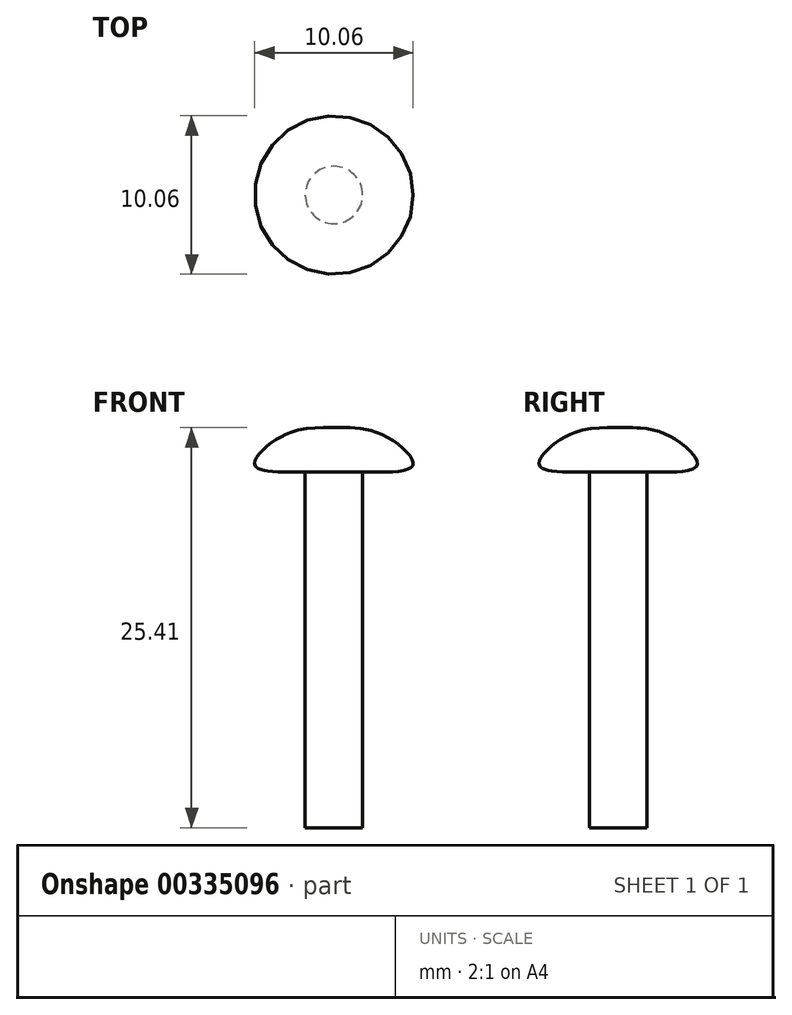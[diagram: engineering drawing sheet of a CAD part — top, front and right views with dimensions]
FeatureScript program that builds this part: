
annotation { "Feature Type Name" : "Feature", "Feature Type Description" : "" }
export const myFeature = defineFeature(function(context is Context, id is Id, definition is map)
    precondition{}
    {
        {
            var Q0;
            Q0=qCreatedBy(makeId("Front.planeOp"),FACE);
            var sketch = newSketch(context, id + "F0", { "sketchPlane" : qUnion([Q0])});
            skFitSpline(sketch, "E0", {"points": [v(0, 25.4) * mm, v(3.16, 24.93) * mm, v(5.03, 23.06) * mm, v(1.82, 22.6) * mm], "startDerivative": vector(9.1, 0.23) * mm, "endDerivative": vector(-13.32, 0.24) * mm});
            skLineSegment(sketch, "E1", {"start": v(1.82, 22.6) * mm, "end": v(1.82, 0) * mm});
            skLineSegment(sketch, "E2", {"start": v(1.82, 0) * mm, "end": v(0, 0) * mm});
            skLineSegment(sketch, "E3", {"start": v(0, 0) * mm, "end": v(0, 25.4) * mm});
            skSolve(sketch);
        }
        {
            var Q0;
            Q0=makeQuery(id+"F0.imprint","IMPRINT",FACE,{"disambiguationData":[TD([[makeQuery(id+"F0.imprint","IMPRINT",EDGE,{"derivedFrom":sQuery(id+"F0.wireOp",EDGE,"E0")}),-1.0]])]});
            var Q1;
            Q1=sQuery(id+"F0.wireOp",EDGE,"E3");
            revolve(context, id + "F1", {"entities" : qUnion([Q0]), "axis" : qUnion([Q1]), "revolveType" : RevolveType.FULL});
        }
        {
            var Q0;
            Q0=qCreatedBy(makeId("Top.planeOp"),FACE);
            cPlane(context, id + "F2", {"entities" : qUnion([Q0]), "cplaneType" : CPlaneType.OFFSET, "offset" : 22.4 * mm, "oppositeDirection" : true, "width" : 152.4 * mm, "height" : 152.4 * mm});
        }
    });
